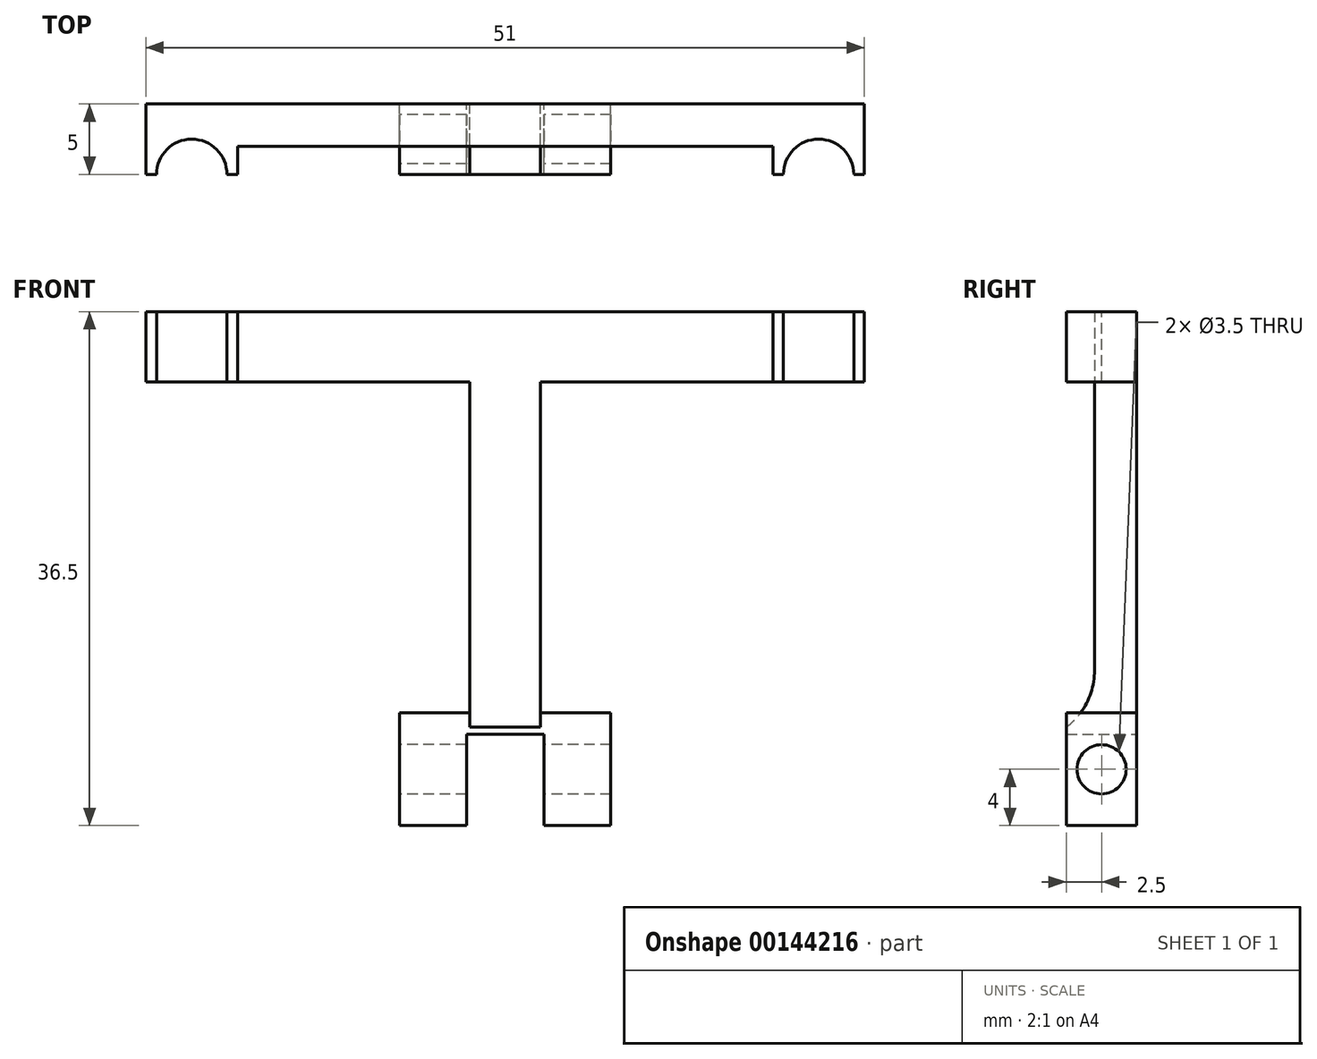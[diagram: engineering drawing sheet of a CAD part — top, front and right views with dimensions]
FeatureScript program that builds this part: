
annotation { "Feature Type Name" : "Feature", "Feature Type Description" : "" }
export const myFeature = defineFeature(function(context is Context, id is Id, definition is map)
    precondition{}
    {
        {
            var Q0;
            Q0=qCreatedBy(makeId("Front.planeOp"),FACE);
            var sketch = newSketch(context, id + "F0", { "sketchPlane" : qUnion([Q0])});
            skLineSegment(sketch, "E0.bottom", {"start": v(2.5, 15) * mm, "end": v(-2.5, 15) * mm});
            skLineSegment(sketch, "E0.top", {"start": v(2.5, -15) * mm, "end": v(-2.5, -15) * mm});
            skLineSegment(sketch, "E0.left", {"start": v(2.5, 15) * mm, "end": v(2.5, -15) * mm});
            skLineSegment(sketch, "E0.right", {"start": v(-2.5, 15) * mm, "end": v(-2.5, -15) * mm});
            skPoint(sketch, "E0.middle", {"position": v(0, 0) * mm});
            skLineSegment(sketch, "E1.bottom", {"start": v(7.5, -19) * mm, "end": v(-7.5, -19) * mm});
            skLineSegment(sketch, "E1.top", {"start": v(7.5, -11) * mm, "end": v(-7.5, -11) * mm});
            skLineSegment(sketch, "E1.left", {"start": v(7.5, -19) * mm, "end": v(7.5, -11) * mm});
            skLineSegment(sketch, "E1.right", {"start": v(-7.5, -19) * mm, "end": v(-7.5, -11) * mm});
            skPoint(sketch, "E1.middle", {"position": v(0, -15) * mm});
            skLineSegment(sketch, "E2.bottom", {"start": v(-25.5, 17.5) * mm, "end": v(25.5, 17.5) * mm});
            skLineSegment(sketch, "E2.top", {"start": v(-25.5, 12.5) * mm, "end": v(25.5, 12.5) * mm});
            skLineSegment(sketch, "E2.left", {"start": v(-25.5, 17.5) * mm, "end": v(-25.5, 12.5) * mm});
            skLineSegment(sketch, "E2.right", {"start": v(25.5, 17.5) * mm, "end": v(25.5, 12.5) * mm});
            skPoint(sketch, "E2.middle", {"position": v(0, 15) * mm});
            skSolve(sketch);
        }
        {
            var Q0;
            Q0 = qSketchRegion(id + "F0", true);
            extrude(context, id + "F1", {"entities" : qUnion([Q0]), "depth" : 5 * mm});
        }
        {
            var Q0;
            Q0=makeQuery(id+"F1.opExtrude","SWEPT_FACE",FACE,{"disambiguationData":[OSD([sQuery(id+"F0.wireOp",EDGE,"E1.bottom")])]});
            var sketch = newSketch(context, id + "F2", { "sketchPlane" : qUnion([Q0])});
            skLineSegment(sketch, "E3.bottom", {"start": v(-2.75, 5) * mm, "end": v(2.75, 5) * mm});
            skLineSegment(sketch, "E3.top", {"start": v(-2.75, -0.68) * mm, "end": v(2.75, -0.68) * mm});
            skLineSegment(sketch, "E3.left", {"start": v(-2.75, 5) * mm, "end": v(-2.75, -0.68) * mm});
            skLineSegment(sketch, "E3.right", {"start": v(2.75, 5) * mm, "end": v(2.75, -0.68) * mm});
            skPoint(sketch, "E3.middle", {"position": v(0, 2.16) * mm});
            skSolve(sketch);
        }
        {
            var Q0;
            Q0 = qSketchRegion(id + "F2", true);
            extrude(context, id + "F3", {"entities" : qUnion([Q0]), "operationType" : NewBodyOperationType.REMOVE, "oppositeDirection" : true, "depth" : 6.5 * mm});
        }
        {
            var Q0;
            Q0=makeQuery(id+"F1.opExtrude","SWEPT_FACE",FACE,{"disambiguationData":[OSD([sQuery(id+"F0.wireOp",EDGE,"E1.right")])]});
            var sketch = newSketch(context, id + "F4", { "sketchPlane" : qUnion([Q0])});
            skLineSegment(sketch, "E4", {"start": v(5, -15) * mm, "end": v(0, -15) * mm, "construction": true});
            skLineSegment(sketch, "E5", {"start": v(2.5, -11) * mm, "end": v(2.5, -19) * mm, "construction": true});
            skCircle(sketch, "E6", {"center": v(2.5, -15) * mm, "radius": 1.75 * mm});
            skSolve(sketch);
        }
        {
            var Q0;
            Q0 = qSketchRegion(id + "F4", true);
            extrude(context, id + "F5", {"entities" : qUnion([Q0]), "operationType" : NewBodyOperationType.REMOVE, "oppositeDirection" : true, "depth" : 25.4 * mm});
        }
        {
            var Q0;
            Q0=makeQuery(id+"F1.opExtrude","CAP_FACE",FACE,{"disambiguationData":[OSD([sQuery(id+"F0.wireOp",EDGE,"E0.left"),sQuery(id+"F0.wireOp",EDGE,"E0.right"),sQuery(id+"F0.wireOp",EDGE,"E1.bottom"),sQuery(id+"F0.wireOp",EDGE,"E1.top"),sQuery(id+"F0.wireOp",EDGE,"E1.left"),sQuery(id+"F0.wireOp",EDGE,"E1.right"),sQuery(id+"F0.wireOp",EDGE,"E2.bottom"),sQuery(id+"F0.wireOp",EDGE,"E2.top"),sQuery(id+"F0.wireOp",EDGE,"E2.left"),sQuery(id+"F0.wireOp",EDGE,"E2.right")])],"isStart":false});
            var sketch = newSketch(context, id + "F6", { "sketchPlane" : qUnion([Q0])});
            skLineSegment(sketch, "E7.bottom", {"start": v(-2.5, -12) * mm, "end": v(2.5, -12) * mm});
            skLineSegment(sketch, "E7.top", {"start": v(-2.5, 17.5) * mm, "end": v(2.5, 17.5) * mm});
            skLineSegment(sketch, "E7.left", {"start": v(-2.5, -12) * mm, "end": v(-2.5, 17.5) * mm});
            skLineSegment(sketch, "E7.right", {"start": v(2.5, -12) * mm, "end": v(2.5, 17.5) * mm});
            skLineSegment(sketch, "E8.bottom", {"start": v(-25.5, 12.5) * mm, "end": v(25.5, 12.5) * mm});
            skLineSegment(sketch, "E8.top", {"start": v(-25.5, 17.5) * mm, "end": v(25.5, 17.5) * mm});
            skLineSegment(sketch, "E8.left", {"start": v(-25.5, 12.5) * mm, "end": v(-25.5, 17.5) * mm});
            skLineSegment(sketch, "E8.right", {"start": v(25.5, 12.5) * mm, "end": v(25.5, 17.5) * mm});
            skSolve(sketch);
        }
        {
            var Q0;
            Q0 = qSketchRegion(id + "F6", true);
            extrude(context, id + "F7", {"entities" : qUnion([Q0]), "operationType" : NewBodyOperationType.REMOVE, "oppositeDirection" : true, "depth" : 2 * mm});
        }
        {
            var Q0;
            Q0=makeQuery(id+"F7.boolean.opBoolean","COPY",EDGE,{"derivedFrom":makeQuery(id+"F7.opExtrude","CAP_EDGE",EDGE,{"disambiguationData":[OSD([sQuery(id+"F6.wireOp",EDGE,"E7.bottom")])],"isStart":false})});
            fillet(context, id + "F8", {"entities" : qUnion([Q0]), "radius" : 5.08 * mm, "tangentPropagation" : true, "allowEdgeOverflow" : false});
        }
        {
            var Q0;
            Q0=makeQuery(id+"F7.boolean.opBoolean","COPY",FACE,{"derivedFrom":makeQuery(id+"F7.opExtrude","CAP_FACE",FACE,{"disambiguationData":[OSD([sQuery(id+"F6.wireOp",EDGE,"E7.bottom"),sQuery(id+"F6.wireOp",EDGE,"E7.left"),sQuery(id+"F6.wireOp",EDGE,"E7.right"),sQuery(id+"F6.wireOp",EDGE,"E8.bottom"),sQuery(id+"F6.wireOp",EDGE,"E8.top"),sQuery(id+"F6.wireOp",EDGE,"E8.left"),sQuery(id+"F6.wireOp",EDGE,"E8.right")])],"isStart":false})});
            var sketch = newSketch(context, id + "F9", { "sketchPlane" : qUnion([Q0])});
            skLineSegment(sketch, "E9.bottom", {"start": v(25.5, 17.5) * mm, "end": v(19, 17.5) * mm});
            skLineSegment(sketch, "E9.top", {"start": v(25.5, 12.5) * mm, "end": v(19, 12.5) * mm});
            skLineSegment(sketch, "E9.left", {"start": v(25.5, 17.5) * mm, "end": v(25.5, 12.5) * mm});
            skLineSegment(sketch, "E9.right", {"start": v(19, 17.5) * mm, "end": v(19, 12.5) * mm});
            skLineSegment(sketch, "E10.MirrorCS", {"start": v(-25.5, 12.5) * mm, "end": v(-19, 12.5) * mm});
            skLineSegment(sketch, "E11.MirrorCS", {"start": v(-19, 17.5) * mm, "end": v(-19, 12.5) * mm});
            skLineSegment(sketch, "E12.MirrorCS", {"start": v(-25.5, 17.5) * mm, "end": v(-19, 17.5) * mm});
            skLineSegment(sketch, "E13.MirrorCS", {"start": v(-25.5, 17.5) * mm, "end": v(-25.5, 12.5) * mm});
            skSolve(sketch);
        }
        {
            var Q0;
            Q0 = qSketchRegion(id + "F9", true);
            extrude(context, id + "F10", {"entities" : qUnion([Q0]), "operationType" : NewBodyOperationType.ADD, "depth" : 2 * mm});
        }
        {
            var Q0;
            Q0=makeQuery(id+"F10.boolean.opBoolean","MERGE",FACE,{"derivedFrom":[makeQuery(id+"F1.opExtrude","SWEPT_FACE",FACE,{"disambiguationData":[OSD([sQuery(id+"F0.wireOp",EDGE,"E2.bottom")])]}),makeQuery(id+"F10.opExtrude","SWEPT_FACE",FACE,{"disambiguationData":[OSD([sQuery(id+"F9.wireOp",EDGE,"E9.bottom")])]})]});
            var sketch = newSketch(context, id + "F11", { "sketchPlane" : qUnion([Q0])});
            skCircle(sketch, "E14", {"center": v(22.25, -5) * mm, "radius": 2.5 * mm});
            skCircle(sketch, "E15.MirrorC", {"center": v(-22.25, -5) * mm, "radius": 2.5 * mm});
            skSolve(sketch);
        }
        {
            var Q0;
            Q0 = qSketchRegion(id + "F11", true);
            extrude(context, id + "F12", {"entities" : qUnion([Q0]), "operationType" : NewBodyOperationType.REMOVE, "endBound" : BoundingType.THROUGH_ALL, "oppositeDirection" : true, "depth" : 25.4 * mm});
        }
    });
